# Revit family: Indoor_Sofa_Santa & Cole_Cadaqués
name_source: partatom
category: Mobiliario
revit_build: Autodesk Revit 2018 (Build: 20190510_1515(x64)
units: mm (PartAtom-declared; Revit-internal decimal feet)

## family parameters
Compartido = No
Corte con vacíos al cargar = No
Número OmniClass = 23.40.20.00
Punto de cálculo de habitación = No
Se basa en plano de trabajo = No
Siempre vertical = Sí
Título OmniClass = General Furniture and Specialties

## types (4) — shared parameters
Fabricante = Santa & Cole
Manufacturer website = https://www.santacole.com
Modelo = Cadaqués
Technical Information = https://www.santacole.com
URL = https://www.santacole.com

## per-type parameters (varying)
| type | Code | Heigth | Length | Ottoman | Sofa | Width |
| Lounge Chair | CAD1x | 750 mm | 1000 mm  [stored 3.28084 ft] | No | Sí | 1000 mm  [stored 3.28084 ft] |
| Two Seat Sofa | CAD2x | 750 mm | 2000 mm | No | Sí | 1000 mm  [stored 3.28084 ft] |
| Three Seat Sofa | CAD3x | 750 mm | 2500 mm  [stored 8.2021 ft] | No | Sí | 1000 mm  [stored 3.28084 ft] |
| Ottoman | CAP0x | 340 mm | 1000 mm  [stored 3.28084 ft] | Sí | No | 750 mm |

note: [stored X ft] marks values corroborated as IEEE doubles in the binary element streams (Revit-internal decimal feet)
